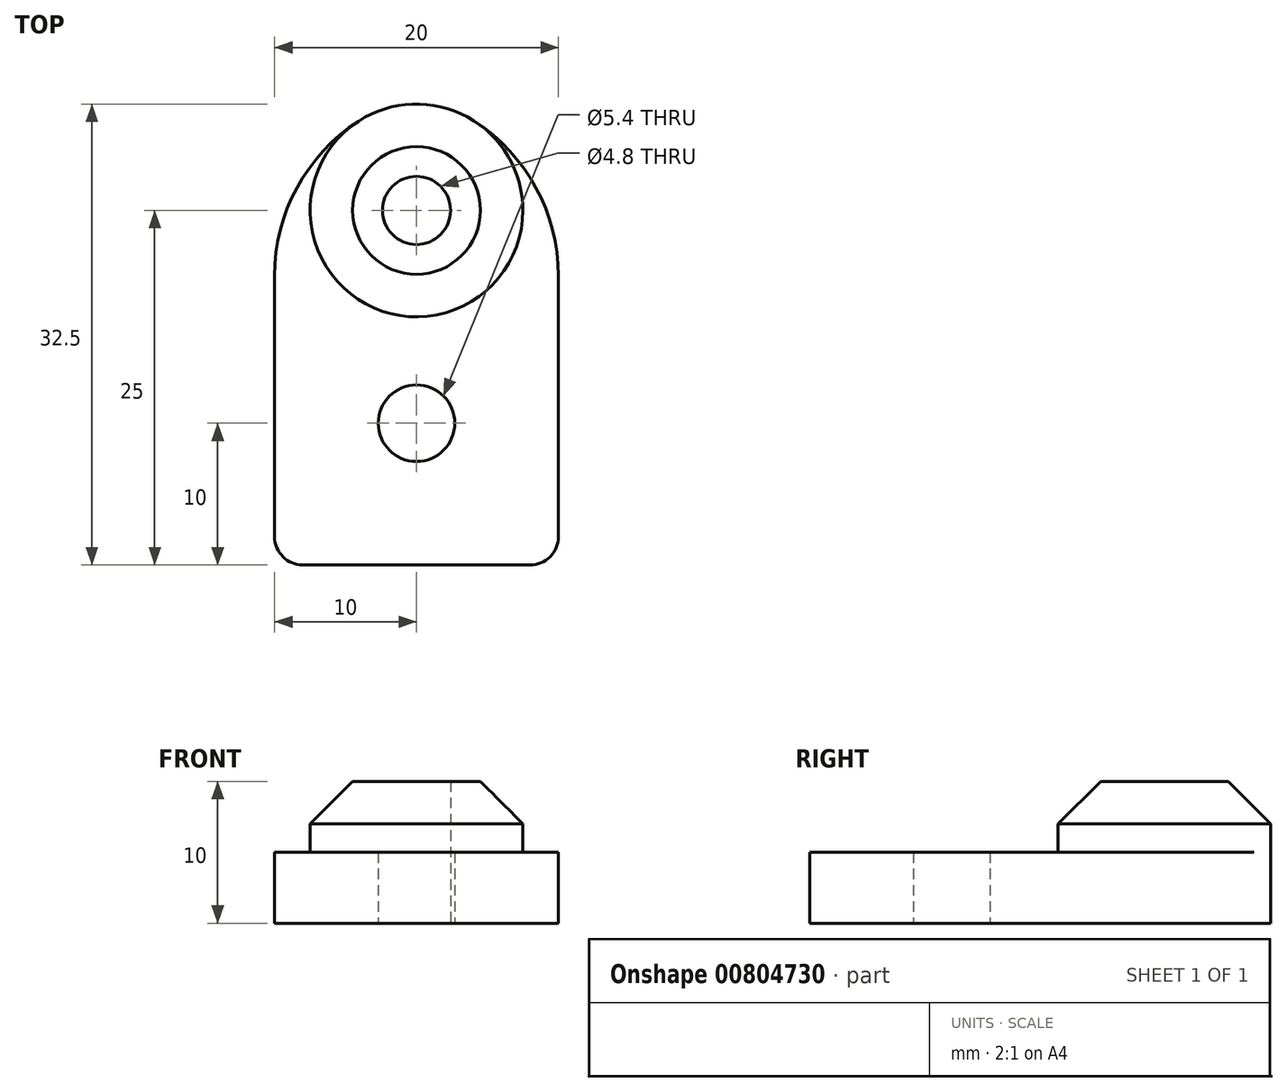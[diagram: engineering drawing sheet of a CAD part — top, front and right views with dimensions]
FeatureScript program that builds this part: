
annotation { "Feature Type Name" : "Feature", "Feature Type Description" : "" }
export const myFeature = defineFeature(function(context is Context, id is Id, definition is map)
    precondition{}
    {
        {
            var Q0;
            Q0=qCreatedBy(makeId("Top.planeOp"),FACE);
            var sketch = newSketch(context, id + "F0", { "sketchPlane" : qUnion([Q0])});
            skLineSegment(sketch, "E0", {"start": v(-10, 0) * mm, "end": v(10, 0) * mm});
            skLineSegment(sketch, "E1", {"start": v(10, 0) * mm, "end": v(10, 20.4) * mm});
            skLineSegment(sketch, "E2", {"start": v(-10, 20.4) * mm, "end": v(-10, 0) * mm});
            skArc(sketch, "E3", {"start": v(-10, 20.4) * mm, "mid": v(-8.42, 26.6) * mm, "end": v(-4.08, 31.3) * mm});
            skArc(sketch, "E4", {"start": v(-4.08, 31.3) * mm, "mid": v(0, 32.5) * mm, "end": v(4.08, 31.3) * mm});
            skArc(sketch, "E5", {"start": v(4.08, 31.3) * mm, "mid": v(8.42, 26.6) * mm, "end": v(10, 20.4) * mm});
            skCircle(sketch, "E6", {"center": v(0, 10) * mm, "radius": 2.7 * mm});
            skLineSegment(sketch, "E7", {"start": v(0, 10) * mm, "end": v(0, 0) * mm, "construction": true});
            skCircle(sketch, "E8", {"center": v(0, 25) * mm, "radius": 2.4 * mm});
            skSolve(sketch);
        }
        {
            var Q0;
            Q0=makeQuery(id+"F0.imprint","IMPRINT",FACE,{"disambiguationData":[TD([[makeQuery(id+"F0.imprint","IMPRINT",EDGE,{"derivedFrom":sQuery(id+"F0.wireOp",EDGE,"E0")}),1.0]])]});
            extrude(context, id + "F1", {"entities" : qUnion([Q0]), "depth" : 5 * mm, "offsetDistance" : 25 * mm});
        }
        {
            var Q0;
            Q0=makeQuery(id+"F1.opExtrude","CAP_FACE",FACE,{"disambiguationData":[OSD([sQuery(id+"F0.wireOp",EDGE,"E0"),sQuery(id+"F0.wireOp",EDGE,"E1"),sQuery(id+"F0.wireOp",EDGE,"E2"),sQuery(id+"F0.wireOp",EDGE,"E3"),sQuery(id+"F0.wireOp",EDGE,"E4"),sQuery(id+"F0.wireOp",EDGE,"E5"),sQuery(id+"F0.wireOp",EDGE,"E6"),sQuery(id+"F0.wireOp",EDGE,"E8")])],"isStart":false});
            var sketch = newSketch(context, id + "F2", { "sketchPlane" : qUnion([Q0])});
            skCircle(sketch, "E9", {"center": v(0, 25) * mm, "radius": 7.5 * mm});
            skCircle(sketch, "E10.0", {"center": v(0, 25) * mm, "radius": 2.4 * mm});
            skSolve(sketch);
        }
        {
            var Q0;
            Q0=qSketchRegion(id+"F2",true);
            extrude(context, id + "F3", {"entities" : qUnion([Q0]), "operationType" : NewBodyOperationType.ADD, "depth" : 5 * mm, "offsetDistance" : 25 * mm});
        }
        {
            var Q0;
            Q0=makeQuery(id+"F3.opExtrude","CAP_EDGE",EDGE,{"disambiguationData":[OSD([sQuery(id+"F2.wireOp",EDGE,"E9")])],"isStart":false});
            chamfer(context, id + "F4", {"entities" : qUnion([Q0]), "width" : 3 * mm, "tangentPropagation" : true});
        }
        {
            var Q0;
            Q0=makeQuery(id+"F1.opExtrude","SWEPT_EDGE",EDGE,{"disambiguationData":[OSD([sQuery(id+"F0.wireOp",EDGE,"E0"),sQuery(id+"F0.wireOp",EDGE,"E2")])]});
            var Q1;
            Q1=makeQuery(id+"F1.opExtrude","SWEPT_EDGE",EDGE,{"disambiguationData":[OSD([sQuery(id+"F0.wireOp",EDGE,"E0"),sQuery(id+"F0.wireOp",EDGE,"E1")])]});
            fillet(context, id + "F5", {"entities" : qUnion([Q0, Q1]), "radius" : 2 * mm, "tangentPropagation" : true, "allowEdgeOverflow" : false});
        }
    });
